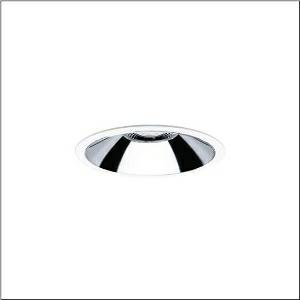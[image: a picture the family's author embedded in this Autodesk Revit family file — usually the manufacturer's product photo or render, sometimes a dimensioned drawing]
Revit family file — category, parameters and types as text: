
# Revit family: lunis_21_xl_51db15df42
name_source: partatom
category: Lighting Fixtures
units: mm (PartAtom-declared; Revit-internal decimal feet)

## family parameters
Cut with Voids When Loaded = No
Host = Face
Light Source = No
Part Type = Normal
Room Calculation Point = No
Round Connector Dimension = Use Diameter
Shared = No

## types (1)
- Lunis 21 XL (1 x LED, 2280 lm, 17.7 W, 4000K)
    Apparent Load = 18 VA
    CIE Flux Codes = 89 99 100 100 100
    Color Rendering = 80
    Color Temperature = 4000K
    Default Elevation = 1800 mm
    Description = Lunis 21,  XL, downlight, of PC, light emission: direct distribution, LED rated luminous flux: 2.280lm, light colour: 840, control gear: ECG DALI, with terminal, 5-pole, mains connection: 220..240V, AC, housing, round, of diecast aluminium, traffic white (RAL 9016), diameter: 213mm, protection rating (complete): IP20, insulation class (complete): insulation class II (safety insulation), certification: CE, impact resistance: IK02, packaging unit: 1 piece
    Height = 0 mm  [stored 0 ft]
    Lamp = 1 x LED
    Lamp Light Flux = 2280 lm
    Lamp Power = 17.7 W
    Lamp count = 1
    Length = 213 mm
    Luminous efficacy = 129 lm/W
    Manufacturer = Siteco
    ModVariant = No
    Model = 51DB15DF42
    Mounting Place = Ceiling
    Mounting Type = Recessed
    Number of Poles = 1
    OnlyDefault = Yes
    Power Factor = 1
    Product Name = Lunis 21 XL
    Product group = downlight | ceiling recessed
    ProductGroupID = 402
    Protection Class = Protection class II
    Protection Degree = IP 20
    RLX_Detail_Level = 1
    RlxData = <blob elided: 27009 chars, md5=f5534932>
    Socket = socket
    Standby Power = 0 W
    System Light Flux = 2280 lm
    System Power = 18 W
    Type Comments = Product without accessories
    Type Image = l_1006990.jpg
    URL = http://relux.com
    VarID = ---
    Voltage = 0 V
    Weight = 0.00 kg
    Width = 0 mm  [stored 0 ft]

note: [stored X ft] marks values corroborated as IEEE doubles in the binary element streams (Revit-internal decimal feet)

## geometry (parser evidence)
native form markers: Blend x4, Sweep x12
no freeform markers — native parametric forms only
